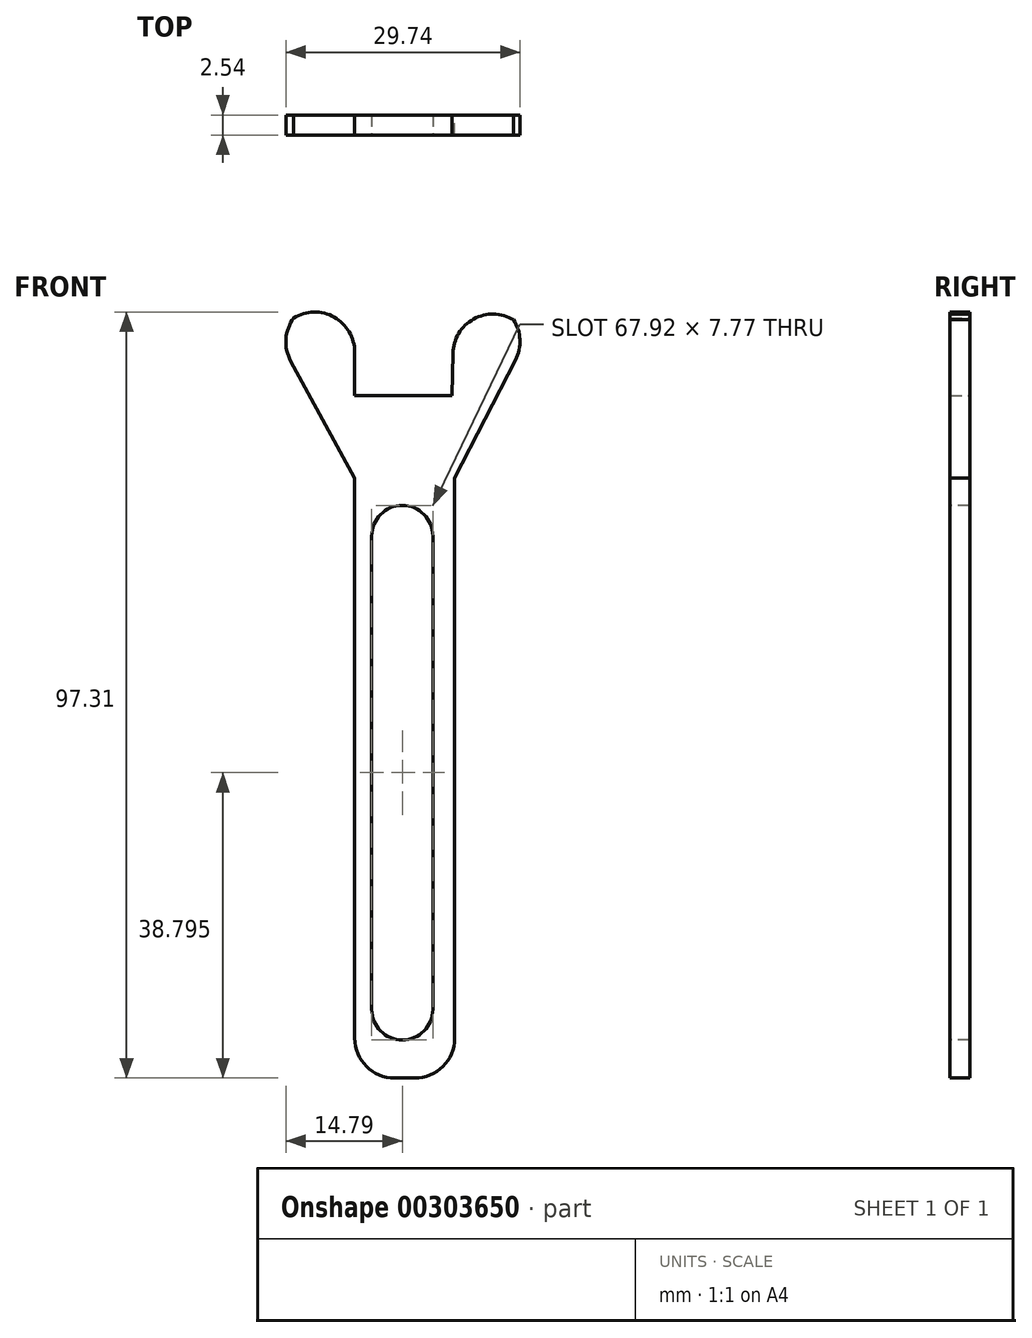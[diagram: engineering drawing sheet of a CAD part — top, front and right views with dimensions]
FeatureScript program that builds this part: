
annotation { "Feature Type Name" : "Feature", "Feature Type Description" : "" }
export const myFeature = defineFeature(function(context is Context, id is Id, definition is map)
    precondition{}
    {
        {
            var Q0;
            Q0=qCreatedBy(makeId("Front.planeOp"),FACE);
            var sketch = newSketch(context, id + "F0", { "sketchPlane" : qUnion([Q0])});
            skLineSegment(sketch, "E0", {"start": v(-49.94, -49.3) * mm, "end": v(-49.94, 26.9) * mm});
            skLineSegment(sketch, "E1", {"start": v(-37.24, -49.3) * mm, "end": v(-37.24, 26.9) * mm});
            skLineSegment(sketch, "E2", {"start": v(-49.94, 26.9) * mm, "end": v(-59.97, 45.3) * mm});
            skLineSegment(sketch, "E3", {"start": v(-59.97, 45.3) * mm, "end": v(-49.94, 54.44) * mm});
            skLineSegment(sketch, "E4", {"start": v(-37.24, 26.9) * mm, "end": v(-27.77, 45.3) * mm});
            skLineSegment(sketch, "E5", {"start": v(-27.77, 45.3) * mm, "end": v(-37.24, 54.44) * mm});
            skLineSegment(sketch, "E6", {"start": v(-49.94, 54.44) * mm, "end": v(-49.94, 37.4) * mm});
            skLineSegment(sketch, "E7", {"start": v(-49.94, 37.4) * mm, "end": v(-37.56, 37.4) * mm});
            skLineSegment(sketch, "E8", {"start": v(-37.56, 37.4) * mm, "end": v(-37.24, 54.44) * mm});
            skLineSegment(sketch, "E9", {"start": v(-49.94, -49.3) * mm, "end": v(-37.24, -49.3) * mm});
            skSolve(sketch);
        }
        {
            var Q0;
            Q0 = qSketchRegion(id + "F0", true);
            extrude(context, id + "F1", {"entities" : qUnion([Q0]), "depth" : 2.54 * mm});
        }
        {
            var Q0;
            Q0=makeQuery(id+"F1.opExtrude","SWEPT_EDGE",EDGE,{"disambiguationData":[OSD([sQuery(id+"F0.wireOp",EDGE,"E4"),sQuery(id+"F0.wireOp",EDGE,"E5")])]});
            var Q1;
            Q1=makeQuery(id+"F1.opExtrude","SWEPT_EDGE",EDGE,{"disambiguationData":[OSD([sQuery(id+"F0.wireOp",EDGE,"E2"),sQuery(id+"F0.wireOp",EDGE,"E3")])]});
            var Q2;
            Q2=makeQuery(id+"F1.opExtrude","SWEPT_EDGE",EDGE,{"disambiguationData":[OSD([sQuery(id+"F0.wireOp",EDGE,"E1"),sQuery(id+"F0.wireOp",EDGE,"E9")])]});
            var Q3;
            Q3=makeQuery(id+"F1.opExtrude","SWEPT_EDGE",EDGE,{"disambiguationData":[OSD([sQuery(id+"F0.wireOp",EDGE,"E0"),sQuery(id+"F0.wireOp",EDGE,"E9")])]});
            var Q4;
            Q4=makeQuery(id+"F1.opExtrude","SWEPT_EDGE",EDGE,{"disambiguationData":[OSD([sQuery(id+"F0.wireOp",EDGE,"E5"),sQuery(id+"F0.wireOp",EDGE,"E8")])]});
            var Q5;
            Q5=makeQuery(id+"F1.opExtrude","SWEPT_EDGE",EDGE,{"disambiguationData":[OSD([sQuery(id+"F0.wireOp",EDGE,"E3"),sQuery(id+"F0.wireOp",EDGE,"E6")])]});
            fillet(context, id + "F2", {"entities" : qUnion([Q0, Q1, Q2, Q3, Q4, Q5]), "radius" : 5.08 * mm, "tangentPropagation" : true, "allowEdgeOverflow" : false});
        }
        {
            var Q0;
            Q0=makeQuery(id+"F1.opExtrude","CAP_FACE",FACE,{"disambiguationData":[OSD([sQuery(id+"F0.wireOp",EDGE,"E0"),sQuery(id+"F0.wireOp",EDGE,"E1"),sQuery(id+"F0.wireOp",EDGE,"E2"),sQuery(id+"F0.wireOp",EDGE,"E3"),sQuery(id+"F0.wireOp",EDGE,"E4"),sQuery(id+"F0.wireOp",EDGE,"E5"),sQuery(id+"F0.wireOp",EDGE,"E6"),sQuery(id+"F0.wireOp",EDGE,"E7"),sQuery(id+"F0.wireOp",EDGE,"E8"),sQuery(id+"F0.wireOp",EDGE,"E9")])],"isStart":false});
            var sketch = newSketch(context, id + "F3", { "sketchPlane" : qUnion([Q0])});
            skLineSegment(sketch, "E10", {"start": v(-40, 19.57) * mm, "end": v(-40, -40.58) * mm});
            skLineSegment(sketch, "E11", {"start": v(-47.78, -40.58) * mm, "end": v(-47.78, 19.57) * mm});
            skArc(sketch, "E12", {"start": v(-47.78, -40.58) * mm, "mid": v(-43.9, -44.47) * mm, "end": v(-40, -40.58) * mm});
            skArc(sketch, "E13", {"start": v(-40, 19.57) * mm, "mid": v(-43.9, 23.46) * mm, "end": v(-47.78, 19.57) * mm});
            skSolve(sketch);
        }
        {
            var Q0;
            Q0=makeQuery(id+"F3.imprint","IMPRINT",FACE,{"disambiguationData":[TD([[makeQuery(id+"F3.imprint","IMPRINT",EDGE,{"derivedFrom":sQuery(id+"F3.wireOp",EDGE,"E10")}),-1.0]])]});
            extrude(context, id + "F4", {"entities" : qUnion([Q0]), "operationType" : NewBodyOperationType.REMOVE, "endBound" : BoundingType.THROUGH_ALL, "oppositeDirection" : true, "depth" : 25.4 * mm});
        }
    });
